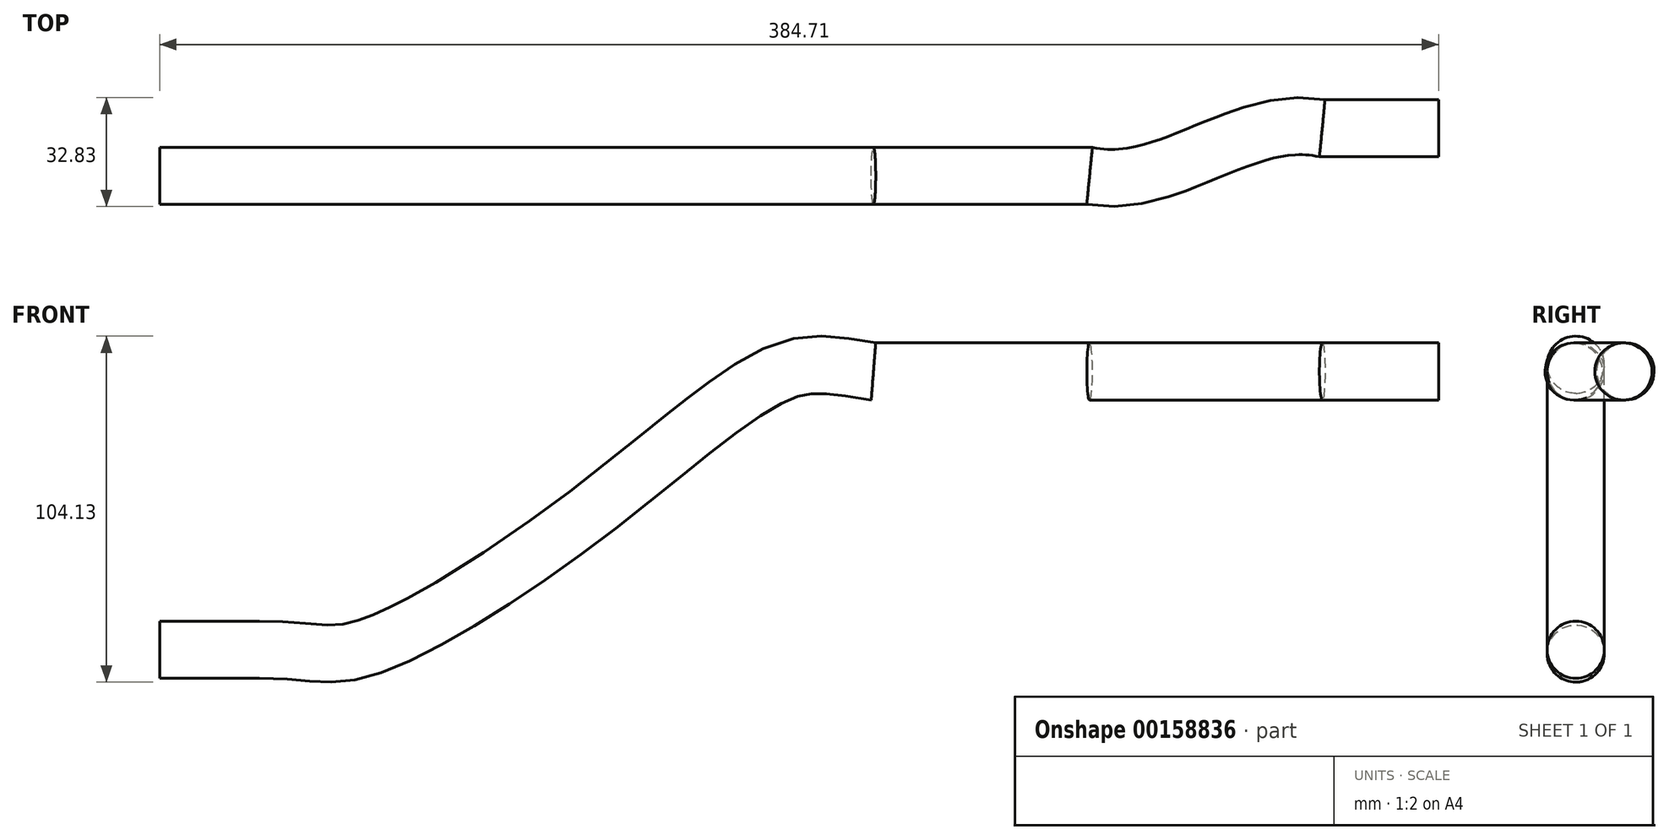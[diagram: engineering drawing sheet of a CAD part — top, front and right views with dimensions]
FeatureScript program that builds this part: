
annotation { "Feature Type Name" : "Feature", "Feature Type Description" : "" }
export const myFeature = defineFeature(function(context is Context, id is Id, definition is map)
    precondition{}
    {
        {
            var Q0;
            Q0=qCreatedBy(makeId("Top.planeOp"),FACE);
            var sketch = newSketch(context, id + "F0", { "sketchPlane" : qUnion([Q0])});
            skLineSegment(sketch, "E0", {"start": v(0, 0) * mm, "end": v(-140, 0) * mm, "construction": true});
            skLineSegment(sketch, "E1", {"start": v(-70, -14.34) * mm, "end": v(-70, 0) * mm, "construction": true});
            skLineSegment(sketch, "E2", {"start": v(-70, -14.34) * mm, "end": v(-140, -14.34) * mm, "construction": true});
            skFitSpline(sketch, "E3", {"points": [v(-35, 0) * mm, v(-70, -7.17) * mm, v(-105, -14.34) * mm], "startDerivative": vector(-70.85, 14.37) * mm, "endDerivative": vector(-70.1, 14.51) * mm});
            skLineSegment(sketch, "E4", {"start": v(-35, 0) * mm, "end": v(0, 0) * mm});
            skLineSegment(sketch, "E5", {"start": v(-105, -14.34) * mm, "end": v(-140, -14.34) * mm});
            skSolve(sketch);
        }
        {
            var Q0;
            Q0=qCreatedBy(makeId("Front.planeOp"),FACE);
            cPlane(context, id + "F1", {"entities" : qUnion([Q0]), "cplaneType" : CPlaneType.OFFSET, "offset" : 14.34 * mm, "width" : 150 * mm, "height" : 150 * mm});
        }
        {
            var Q0;
            Q0=qCreatedBy(id+"F1.planeOp",FACE);
            var sketch = newSketch(context, id + "F2", { "sketchPlane" : qUnion([Q0])});
            skLineSegment(sketch, "E6", {"start": v(-254.71, 0) * mm, "end": v(-140, 0) * mm, "construction": true});
            skLineSegment(sketch, "E7", {"start": v(-254.71, 0) * mm, "end": v(-254.71, -83.73) * mm, "construction": true});
            skLineSegment(sketch, "E8", {"start": v(-254.71, -83.73) * mm, "end": v(-384.71, -83.73) * mm, "construction": true});
            skPoint(sketch, "E9.2.internal.orphan", {"position": v(-254.71, -41.87) * mm});
            skPoint(sketch, "E9.6.internal.orphan", {"position": v(-170.52, 0) * mm});
            skFitSpline(sketch, "E10", {"points": [v(-354.71, -83.73) * mm, v(-324.63, -83.73) * mm, v(-254.71, -41.87) * mm, v(-197.36, 0) * mm, v(-170, 0) * mm], "startDerivative": vector(239.18, 0) * mm, "endDerivative": vector(192.7, -30.34) * mm});
            skLineSegment(sketch, "E11", {"start": v(-170, 0) * mm, "end": v(-140, 0) * mm});
            skLineSegment(sketch, "E12", {"start": v(-384.71, -83.73) * mm, "end": v(-354.71, -83.73) * mm});
            skSolve(sketch);
        }
        {
            var Q0;
            Q0=qCreatedBy(makeId("Right.planeOp"),FACE);
            var sketch = newSketch(context, id + "F3", { "sketchPlane" : qUnion([Q0])});
            skCircle(sketch, "E13", {"center": v(0, 0) * mm, "radius": 8.6 * mm});
            skSolve(sketch);
        }
        {
            var Q0;
            Q0 = qSketchRegion(id + "F3", true);
            var Q1;
            Q1=sQuery(id+"F0.wireOp",EDGE,"E4");
            var Q2;
            Q2=sQuery(id+"F0.wireOp",EDGE,"E3");
            var Q3;
            Q3=sQuery(id+"F0.wireOp",EDGE,"E5");
            var Q4;
            Q4=sQuery(id+"F2.wireOp",EDGE,"E11");
            var Q5;
            Q5=sQuery(id+"F2.wireOp",EDGE,"E10");
            var Q6;
            Q6=sQuery(id+"F2.wireOp",EDGE,"E12");
            sweep(context, id + "F4", {"profiles" : qUnion([Q0]), "path" : qUnion([Q1, Q2, Q3, Q4, Q5, Q6])});
        }
    });
